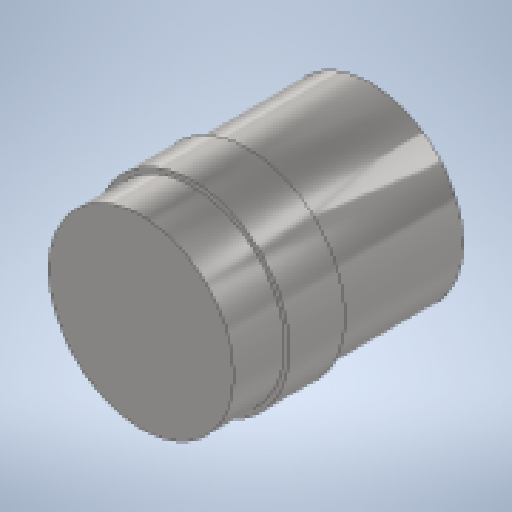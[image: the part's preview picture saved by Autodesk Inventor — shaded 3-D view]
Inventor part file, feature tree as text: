
AUTODESK INVENTOR PART (.ipt)
format: ipt  version: 2023 (Build 270158000, 158)  size: 265,728 bytes
history: native  units: mm
features: extrude x3, sketch x3, plane x1
ambient origin geometry x8: Origin, YZ Plane, XZ Plane, XY Plane, X Axis, Y Axis, Z Axis, Center Point
bodies: Solid1 (feature_tree)
feature tree (7):
  extrude  "Extrusion1"  Depth=37.22mm TaperAngle=0.0deg
  plane  "Work Plane1"
  extrude  "Extrusion2"  Depth=20.0mm
  extrude  "Extrusion3"  Depth=12.0mm
  sketch  "Sketch1"  dims[d0=30.0mm d1=37.22mm d2=0.0mm]
  sketch  "Sketch2"  dims[d3=20.0mm d4=31.7mm]
  sketch  "Sketch3"  dims[d5=9.0mm d6=0.0mm d7=23.5mm d8=12.0mm d9=0.0mm]
